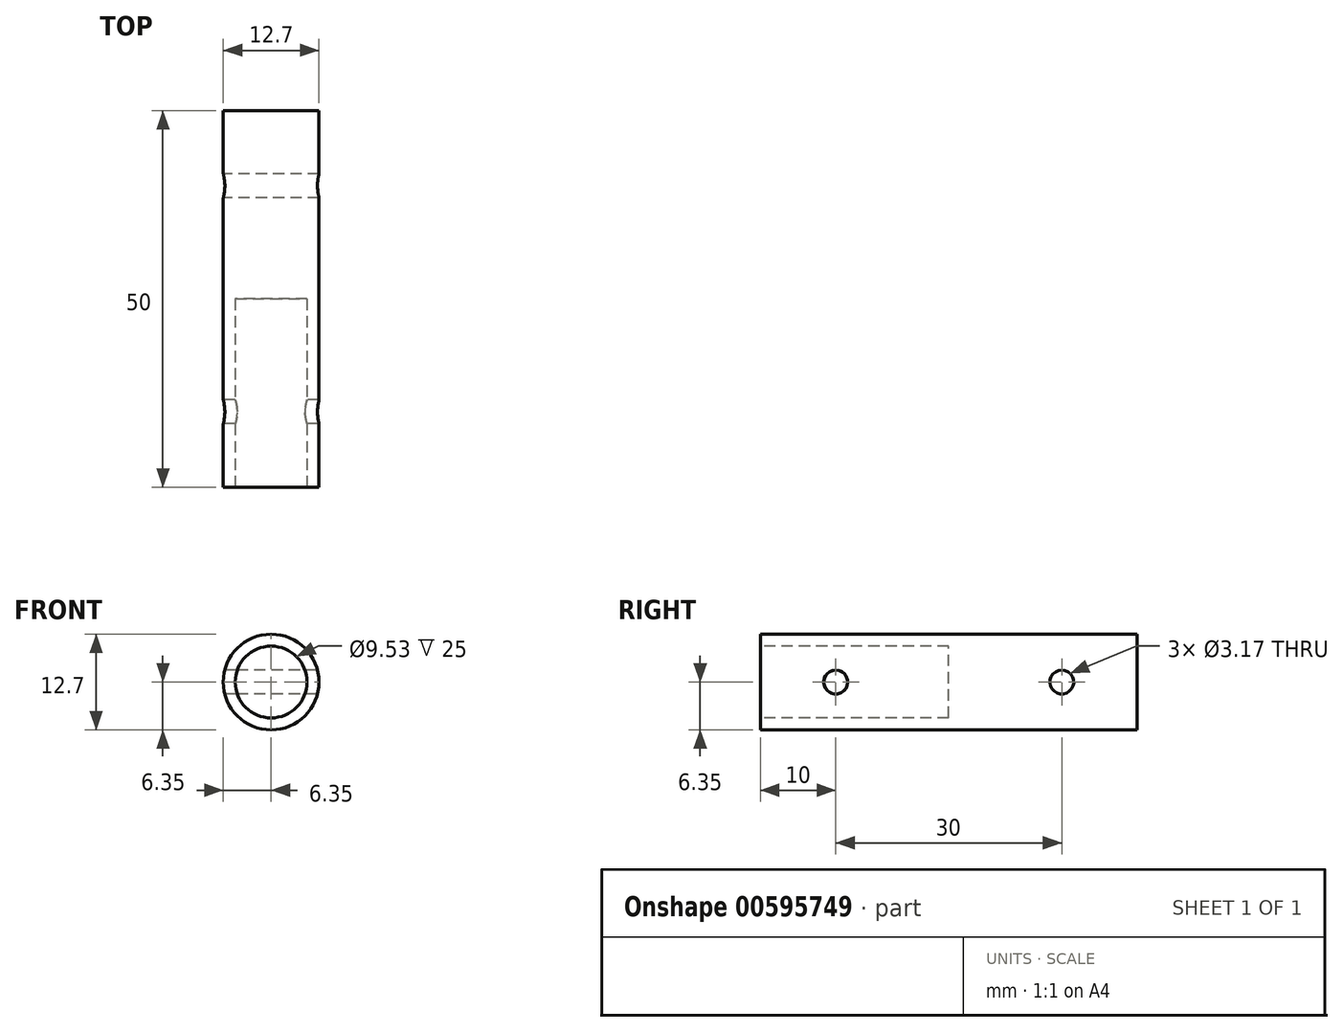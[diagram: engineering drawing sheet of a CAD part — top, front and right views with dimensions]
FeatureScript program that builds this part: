
annotation { "Feature Type Name" : "Feature", "Feature Type Description" : "" }
export const myFeature = defineFeature(function(context is Context, id is Id, definition is map)
    precondition{}
    {
        {
            var Q0;
            Q0=qCreatedBy(makeId("Front.planeOp"),FACE);
            var sketch = newSketch(context, id + "F0", { "sketchPlane" : qUnion([Q0])});
            skCircle(sketch, "E0", {"center": v(0, 0) * mm, "radius": 6.35 * mm});
            skSolve(sketch);
        }
        {
            var Q0;
            Q0=makeQuery(id+"F0.imprint","IMPRINT",FACE,{"disambiguationData":[TD([[makeQuery(id+"F0.imprint","IMPRINT",EDGE,{"derivedFrom":sQuery(id+"F0.wireOp",EDGE,"E0")}),1.0]])]});
            extrude(context, id + "F1", {"entities" : qUnion([Q0]), "depth" : 50 * mm, "offsetDistance" : 25 * mm});
        }
        {
            var Q0;
            Q0=qCreatedBy(makeId("Right.planeOp"),FACE);
            var sketch = newSketch(context, id + "F2", { "sketchPlane" : qUnion([Q0])});
            skPoint(sketch, "E1", {"position": v(-10, 0) * mm});
            skCircle(sketch, "E2", {"center": v(-10, 0) * mm, "radius": 1.59 * mm});
            skCircle(sketch, "E3", {"center": v(-40, 0) * mm, "radius": 1.59 * mm});
            skSolve(sketch);
        }
        {
            var Q0;
            Q0 = qSketchRegion(id + "F2", true);
            extrude(context, id + "F3", {"entities" : qUnion([Q0]), "operationType" : NewBodyOperationType.REMOVE, "depth" : 25 * mm, "offsetDistance" : 25 * mm, "symmetric" : true});
        }
        {
            var Q0;
            Q0=makeQuery(id+"F1.opExtrude","CAP_FACE",FACE,{"disambiguationData":[OSD([sQuery(id+"F0.wireOp",EDGE,"E0")])],"isStart":false});
            var sketch = newSketch(context, id + "F4", { "sketchPlane" : qUnion([Q0])});
            skCircle(sketch, "E4", {"center": v(0, 0) * mm, "radius": 4.76 * mm});
            skSolve(sketch);
        }
        {
            var Q0;
            Q0=makeQuery(id+"F4.imprint","IMPRINT",FACE,{"disambiguationData":[TD([[makeQuery(id+"F4.imprint","IMPRINT",EDGE,{"derivedFrom":sQuery(id+"F4.wireOp",EDGE,"E4")}),1.0]])]});
            extrude(context, id + "F5", {"entities" : qUnion([Q0]), "operationType" : NewBodyOperationType.REMOVE, "oppositeDirection" : true, "depth" : 25 * mm, "offsetDistance" : 25 * mm});
        }
    });
